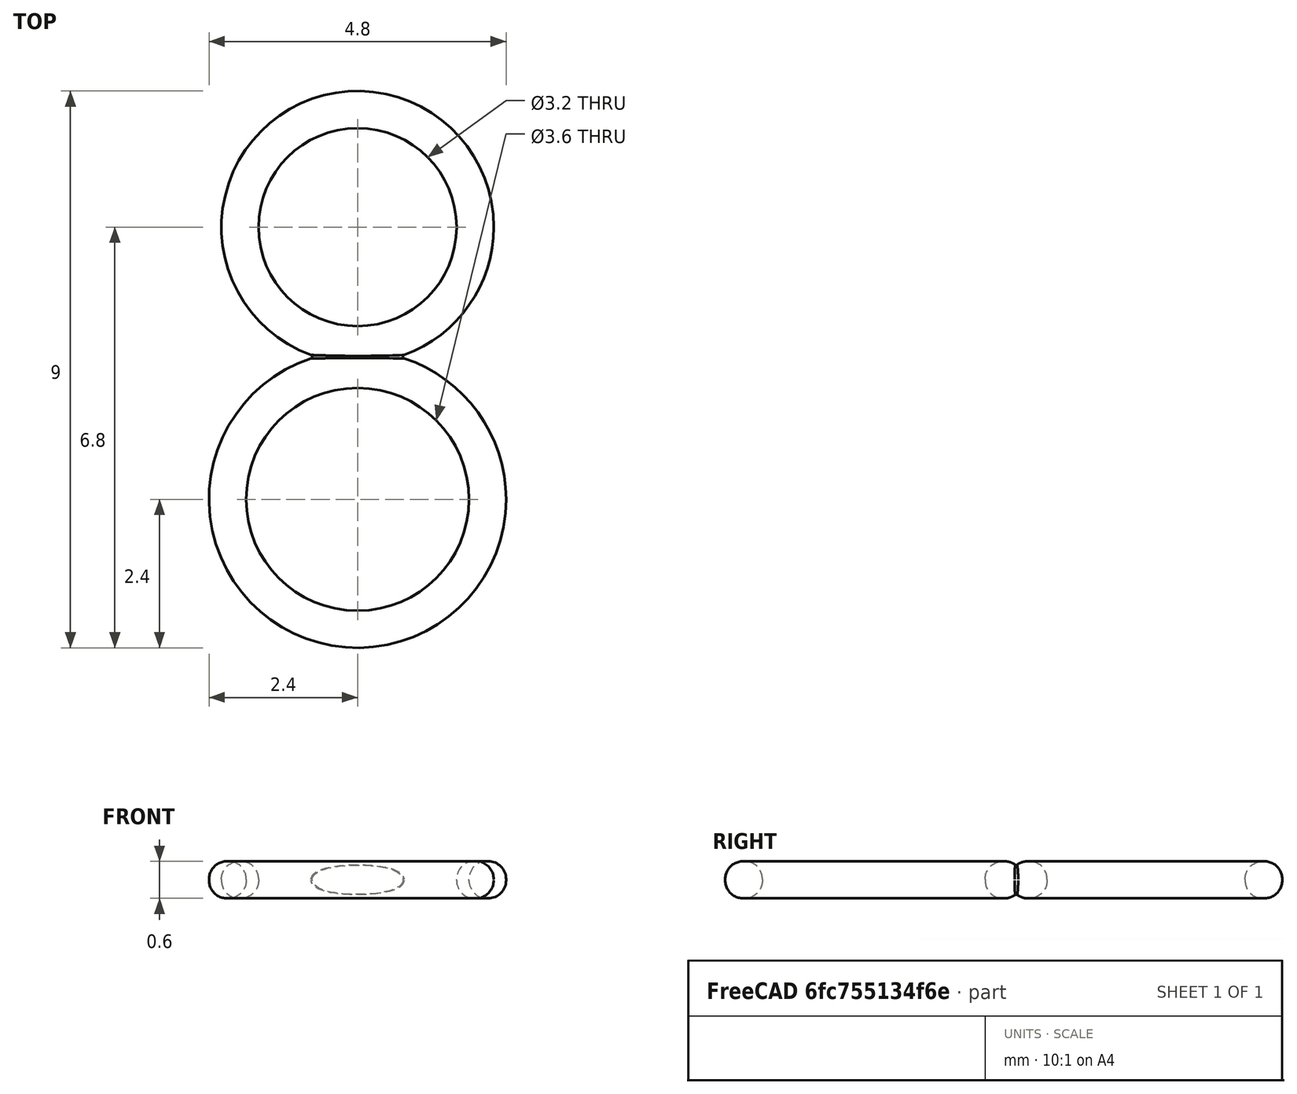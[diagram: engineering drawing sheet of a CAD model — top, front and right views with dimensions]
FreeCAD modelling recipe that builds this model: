
FCSTD DOCUMENT  (FreeCAD 0.16R6712 (Git))
Label: 8s
License: All rights reserved
LicenseURL: http://en.wikipedia.org/wiki/All_rights_reserved
objects: PartDesign::Fillet×3, Sketcher::SketchObject×2, PartDesign::Pad×2, Part::MultiFuse×1, Mesh::Feature×1
note: 10 computed .brp shape members not serialized (recipe doc carries the construction recipe); baked Part::Feature solids carry a one-line shape summary decoded from their .brp

FEATURE [Sketcher::SketchObject] Sketch
  sketch-geometry (2):
    g0: Circle CenterX=0 CenterY=2.4 CenterZ=0 NormalX=0 NormalY=0 NormalZ=1 Radius=1.8
    g1: Circle CenterX=0 CenterY=2.4 CenterZ=0 NormalX=0 NormalY=0 NormalZ=1 Radius=2.4
  constraints (5):
    c: Coincident(g1,g0)
    c: Radius(g1) = 2.4
    c: Radius(g0) = 1.8
    c: Tangent(g1,g-1)
    c: PointOnObject(g0,g-2)
FEATURE [PartDesign::Pad] Pad
  Length = 0.6
  Length2 = 100
  Midplane = true
  Sketch = -> Sketch
  Type = 0
FEATURE [Sketcher::SketchObject] Sketch001
  sketch-geometry (2):
    g0: Circle CenterX=0 CenterY=6.8 CenterZ=0 NormalX=0 NormalY=0 NormalZ=1 Radius=2.2
    g1: Circle CenterX=0 CenterY=6.8 CenterZ=0 NormalX=0 NormalY=0 NormalZ=1 Radius=1.6
  constraints (5):
    c: Coincident(g1,g0)
    c: PointOnObject(g0,g-2)
    c: Radius(g0) = 2.2
    c: Radius(g1) = 1.6
    c: DistanceY(g-1,g0) = 6.8
FEATURE [PartDesign::Pad] Pad001
  Length = 0.6
  Length2 = 100
  Midplane = true
  Sketch = -> Sketch001
  Type = 0
FEATURE [PartDesign::Fillet] Fillet
  Base = -> Pad001 [Edge2,Edge5,Edge3,Edge6]
  Radius = 0.29
FEATURE [PartDesign::Fillet] Fillet001
  Base = -> Pad [Edge2,Edge5,Edge3,Edge6]
  Radius = 0.29
FEATURE [Part::MultiFuse] Fusion
  Shapes = -> [Fillet,Fillet001]
FEATURE [PartDesign::Fillet] Fillet002
  Base = -> Fusion [Edge20,Edge16,Edge4,Edge11]
  Radius = 0.029
FEATURE [Mesh::Feature] Mesh  label="Fillet002 (Meshed)"
